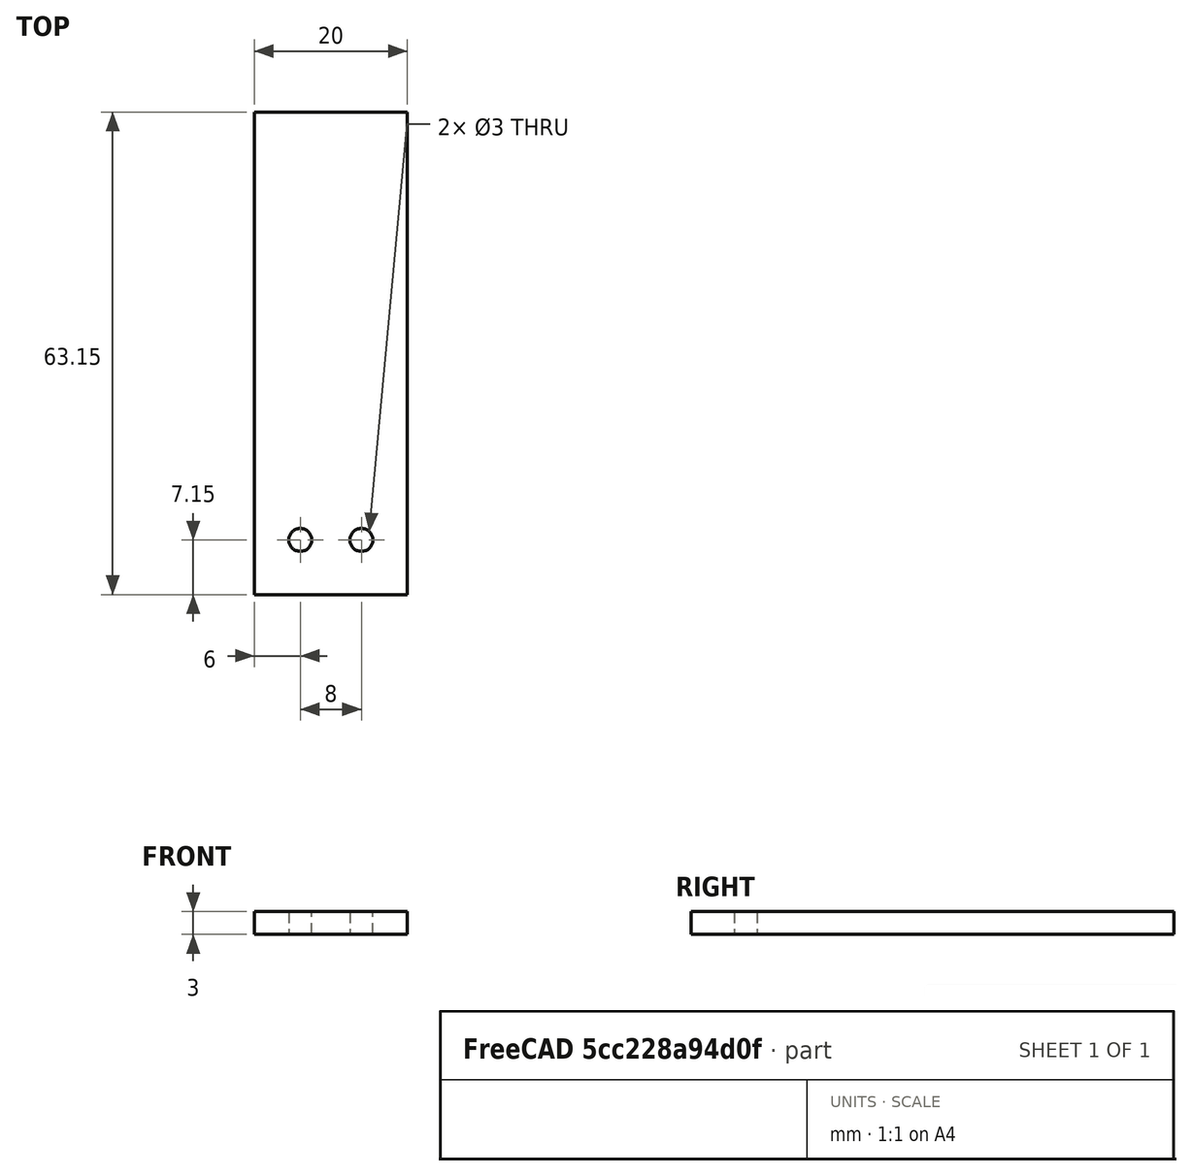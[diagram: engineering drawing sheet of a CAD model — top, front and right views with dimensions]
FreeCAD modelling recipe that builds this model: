
FCSTD DOCUMENT  (FreeCAD 0.16R6707 (Git))
Label: butée
License: All rights reserved
LicenseURL: http://en.wikipedia.org/wiki/All_rights_reserved
objects: Sketcher::SketchObject×1, PartDesign::Pad×1
note: 3 computed .brp shape members not serialized (recipe doc carries the construction recipe); baked Part::Feature solids carry a one-line shape summary decoded from their .brp

FEATURE [Sketcher::SketchObject] Sketch
  sketch-geometry (8):
    g0: LineSegment StartX=0 StartY=0 StartZ=0 EndX=20 EndY=0 EndZ=0
    g1: LineSegment StartX=20 StartY=0 StartZ=0 EndX=20 EndY=63.15 EndZ=0
    g2: LineSegment StartX=20 StartY=63.15 StartZ=0 EndX=0 EndY=63.15 EndZ=0
    g3: LineSegment StartX=0 StartY=63.15 StartZ=0 EndX=0 EndY=0 EndZ=0
    g4: GeomPoint [constr] X=6 Y=7.15 Z=0
    g5: GeomPoint [constr] X=14 Y=7.15 Z=0
    g6: Circle CenterX=6 CenterY=7.15 CenterZ=0 NormalX=0 NormalY=0 NormalZ=1 Radius=1.5
    g7: Circle CenterX=14 CenterY=7.15 CenterZ=0 NormalX=0 NormalY=0 NormalZ=1 Radius=1.5
  constraints (19):
    c: Coincident(g0,g1)
    c: Coincident(g1,g2)
    c: Coincident(g2,g3)
    c: Coincident(g3,g0)
    c: Horizontal(g0)
    c: Horizontal(g2)
    c: Vertical(g1)
    c: Vertical(g3)
    c: Coincident(g0,g-1)
    c: DistanceY(g3,g3) = 63.15
    c: Distance(g2) = 20
    c: DistanceX(g4) = 6
    c: DistanceX(g5,g0) = 6
    c: DistanceY(g5,g4) = 0
    c: DistanceY(g-1,g4) = 7.15
    c: Coincident(g6,g4)
    c: Coincident(g7,g5)
    c: Radius(g6) = 1.5
    c: Equal(g6,g7)
FEATURE [PartDesign::Pad] Pad
  Length = 3
  Length2 = 100
  Sketch = -> Sketch
  Type = 0
